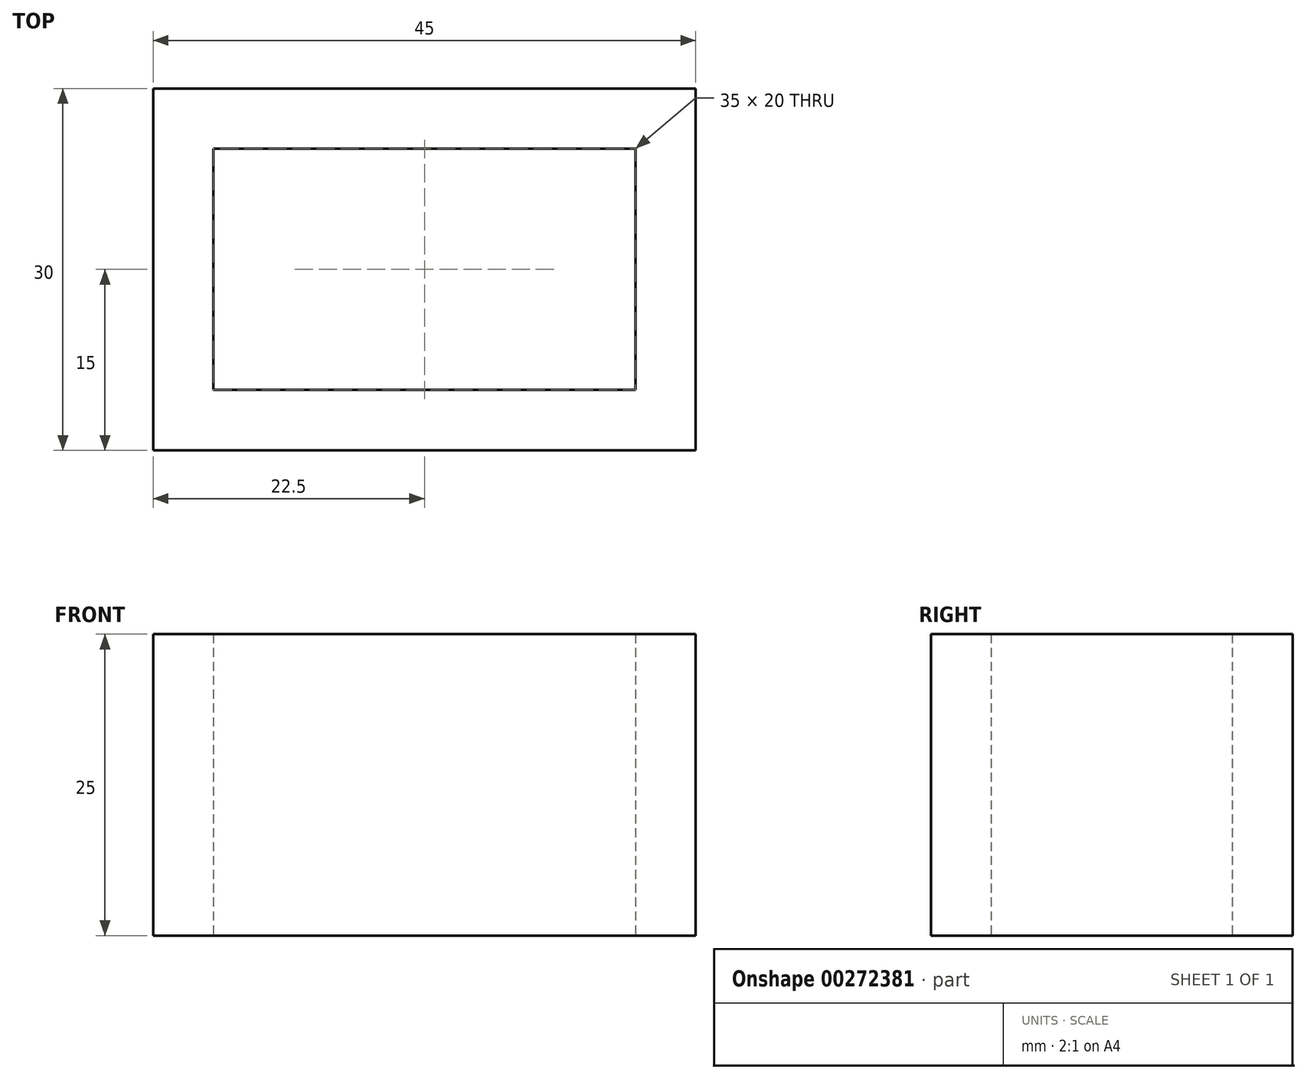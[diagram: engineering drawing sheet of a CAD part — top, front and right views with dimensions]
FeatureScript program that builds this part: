
annotation { "Feature Type Name" : "Feature", "Feature Type Description" : "" }
export const myFeature = defineFeature(function(context is Context, id is Id, definition is map)
    precondition{}
    {
        {
            var Q0;
            Q0=qCreatedBy(makeId("Top.planeOp"),FACE);
            var sketch = newSketch(context, id + "F0", { "sketchPlane" : qUnion([Q0])});
            skLineSegment(sketch, "E0.bottom", {"start": v(-17.5, 10) * mm, "end": v(17.5, 10) * mm});
            skLineSegment(sketch, "E0.top", {"start": v(-17.5, -10) * mm, "end": v(17.5, -10) * mm});
            skLineSegment(sketch, "E0.left", {"start": v(-17.5, 10) * mm, "end": v(-17.5, -10) * mm});
            skLineSegment(sketch, "E0.right", {"start": v(17.5, 10) * mm, "end": v(17.5, -10) * mm});
            skPoint(sketch, "E0.middle", {"position": v(0, 0) * mm});
            skSolve(sketch);
        }
        {
            var Q0;
            Q0=makeQuery(id+"F0.imprint","IMPRINT",FACE,{"disambiguationData":[TD([[makeQuery(id+"F0.imprint","IMPRINT",EDGE,{"derivedFrom":sQuery(id+"F0.wireOp",EDGE,"E0.bottom")}),-1.0]])]});
            var sketch = newSketch(context, id + "F1", { "sketchPlane" : qUnion([Q0])});
            skLineSegment(sketch, "E1.0", {"start": v(-22.5, 15) * mm, "end": v(-22.5, -15) * mm});
            skLineSegment(sketch, "E1.1", {"start": v(22.5, 15) * mm, "end": v(-22.5, 15) * mm});
            skLineSegment(sketch, "E1.2", {"start": v(22.5, -15) * mm, "end": v(22.5, 15) * mm});
            skLineSegment(sketch, "E1.3", {"start": v(-22.5, -15) * mm, "end": v(22.5, -15) * mm});
            skSolve(sketch);
        }
        {
            var Q0;
            Q0=makeQuery(id+"F1.imprint","IMPRINT",FACE,{"disambiguationData":[TD([[makeQuery(id+"F1.imprint","IMPRINT",EDGE,{"derivedFrom":sQuery(id+"F1.wireOp",EDGE,"E1.0")}),1.0]])]});
            extrude(context, id + "F2", {"entities" : qUnion([Q0]), "depth" : 25 * mm});
        }
    });
